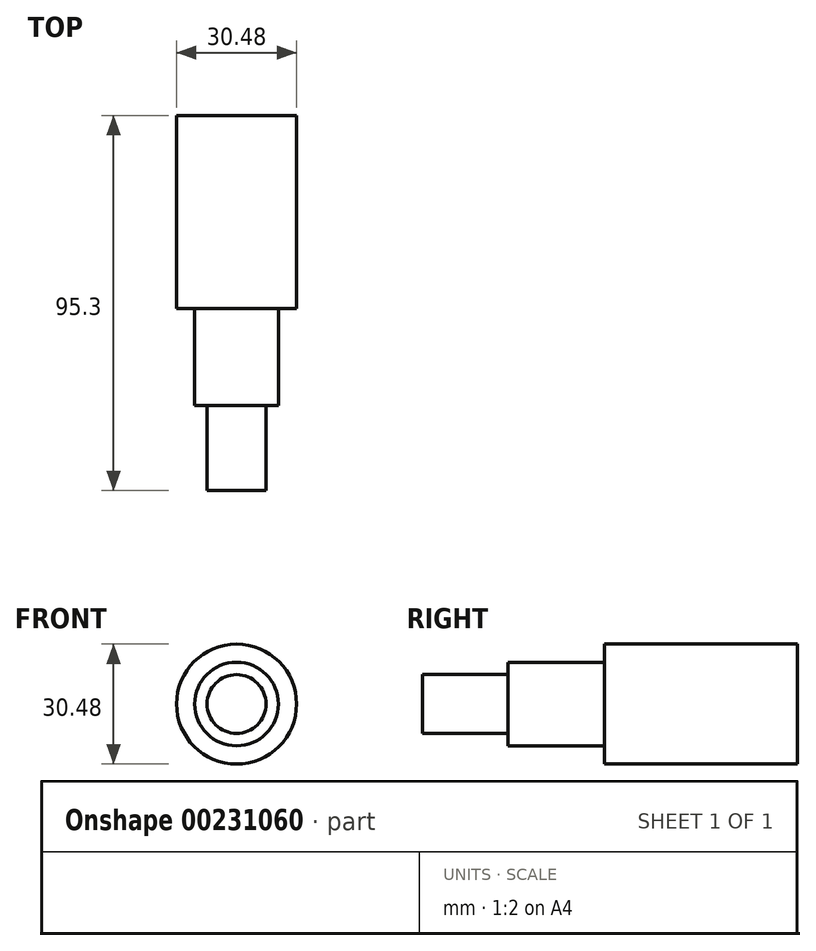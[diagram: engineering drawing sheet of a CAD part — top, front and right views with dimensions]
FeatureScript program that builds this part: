
annotation { "Feature Type Name" : "Feature", "Feature Type Description" : "" }
export const myFeature = defineFeature(function(context is Context, id is Id, definition is map)
    precondition{}
    {
        {
            var Q0;
            Q0=qCreatedBy(makeId("Front.planeOp"),FACE);
            var sketch = newSketch(context, id + "F0", { "sketchPlane" : qUnion([Q0])});
            skCircle(sketch, "E0", {"center": v(0, 0) * mm, "radius": 15.24 * mm});
            skSolve(sketch);
        }
        {
            var Q0;
            Q0 = qSketchRegion(id + "F0", true);
            extrude(context, id + "F1", {"entities" : qUnion([Q0]), "depth" : 49.1 * mm});
        }
        {
            var Q0;
            Q0=makeQuery(id+"F1.opExtrude","CAP_FACE",FACE,{"disambiguationData":[OSD([sQuery(id+"F0.wireOp",EDGE,"E0")])],"isStart":false});
            var sketch = newSketch(context, id + "F2", { "sketchPlane" : qUnion([Q0])});
            skCircle(sketch, "E1", {"center": v(0, 0) * mm, "radius": 10.62 * mm});
            skSolve(sketch);
        }
        {
            var Q0;
            Q0=makeQuery(id+"F2.imprint","IMPRINT",FACE,{"disambiguationData":[TD([[makeQuery(id+"F2.imprint","IMPRINT",EDGE,{"derivedFrom":sQuery(id+"F2.wireOp",EDGE,"E1")}),1.0]])]});
            extrude(context, id + "F3", {"entities" : qUnion([Q0]), "operationType" : NewBodyOperationType.ADD, "depth" : 24.55 * mm});
        }
        {
            var Q0;
            Q0=makeQuery(id+"F3.opExtrude","CAP_FACE",FACE,{"disambiguationData":[OSD([sQuery(id+"F2.wireOp",EDGE,"E1")])],"isStart":false});
            var sketch = newSketch(context, id + "F4", { "sketchPlane" : qUnion([Q0])});
            skCircle(sketch, "E2", {"center": v(0, 0) * mm, "radius": 7.47 * mm});
            skSolve(sketch);
        }
        {
            var Q0;
            Q0=makeQuery(id+"F4.imprint","IMPRINT",FACE,{"disambiguationData":[TD([[makeQuery(id+"F4.imprint","IMPRINT",EDGE,{"derivedFrom":sQuery(id+"F4.wireOp",EDGE,"E2")}),1.0]])]});
            extrude(context, id + "F5", {"entities" : qUnion([Q0]), "operationType" : NewBodyOperationType.ADD, "depth" : 21.65 * mm});
        }
    });
